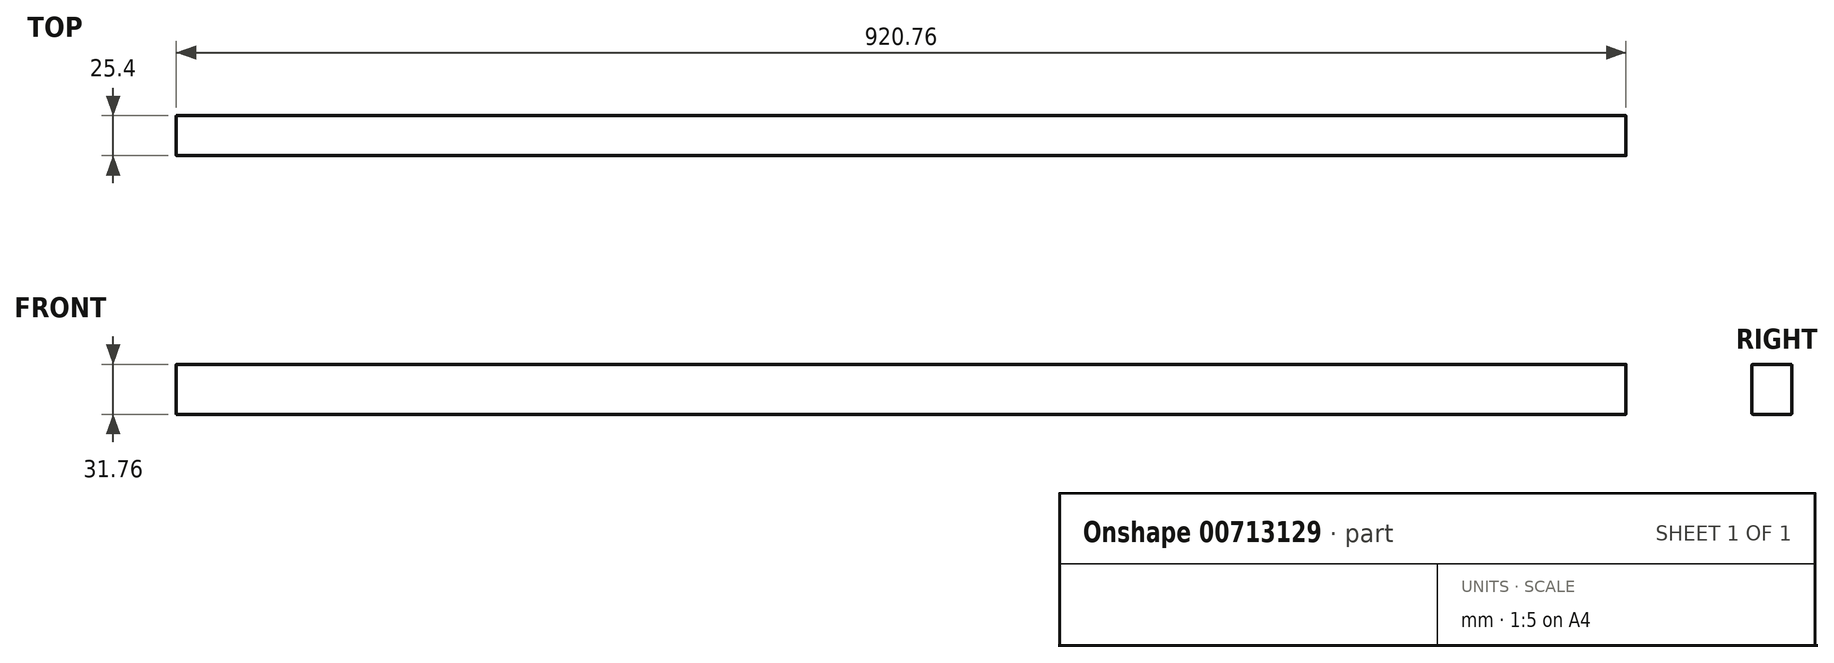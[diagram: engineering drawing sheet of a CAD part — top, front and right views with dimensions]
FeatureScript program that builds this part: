
annotation { "Feature Type Name" : "Feature", "Feature Type Description" : "" }
export const myFeature = defineFeature(function(context is Context, id is Id, definition is map)
    precondition{}
    {
        {
            var Q0;
            Q0=qCreatedBy(makeId("Front.planeOp"),FACE);
            var sketch = newSketch(context, id + "F0", { "sketchPlane" : qUnion([Q0])});
            skLineSegment(sketch, "E0.bottom", {"start": v(-460.38, 15.87) * mm, "end": v(460.38, 15.87) * mm});
            skLineSegment(sketch, "E0.top", {"start": v(-460.38, -15.88) * mm, "end": v(460.38, -15.88) * mm});
            skLineSegment(sketch, "E0.left", {"start": v(-460.38, 15.87) * mm, "end": v(-460.38, -15.88) * mm});
            skLineSegment(sketch, "E0.right", {"start": v(460.38, 15.87) * mm, "end": v(460.38, -15.88) * mm});
            skPoint(sketch, "E0.middle", {"position": v(0, 0) * mm});
            skSolve(sketch);
        }
        {
            var Q0;
            Q0 = qSketchRegion(id + "F0", true);
            extrude(context, id + "F1", {"entities" : qUnion([Q0]), "depth" : 25.4 * mm, "offsetDistance" : 25.4 * mm});
        }
        {
            var Q0;
            Q0=makeQuery(id+"F1.opExtrude","CAP_EDGE",EDGE,{"disambiguationData":[OSD([sQuery(id+"F0.wireOp",EDGE,"E0.bottom")])],"isStart":false});
            var Q1;
            Q1=makeQuery(id+"F1.opExtrude","CAP_EDGE",EDGE,{"disambiguationData":[OSD([sQuery(id+"F0.wireOp",EDGE,"E0.top")])],"isStart":false});
            var Q2;
            Q2=makeQuery(id+"F1.opExtrude","CAP_EDGE",EDGE,{"disambiguationData":[OSD([sQuery(id+"F0.wireOp",EDGE,"E0.bottom")])],"isStart":true});
            var Q3;
            Q3=makeQuery(id+"F1.opExtrude","CAP_EDGE",EDGE,{"disambiguationData":[OSD([sQuery(id+"F0.wireOp",EDGE,"E0.top")])],"isStart":true});
            fillet(context, id + "F2", {"entities" : qUnion([Q0, Q1, Q2, Q3]), "radius" : 0.64 * mm, "tangentPropagation" : true, "allowEdgeOverflow" : false});
        }
    });
